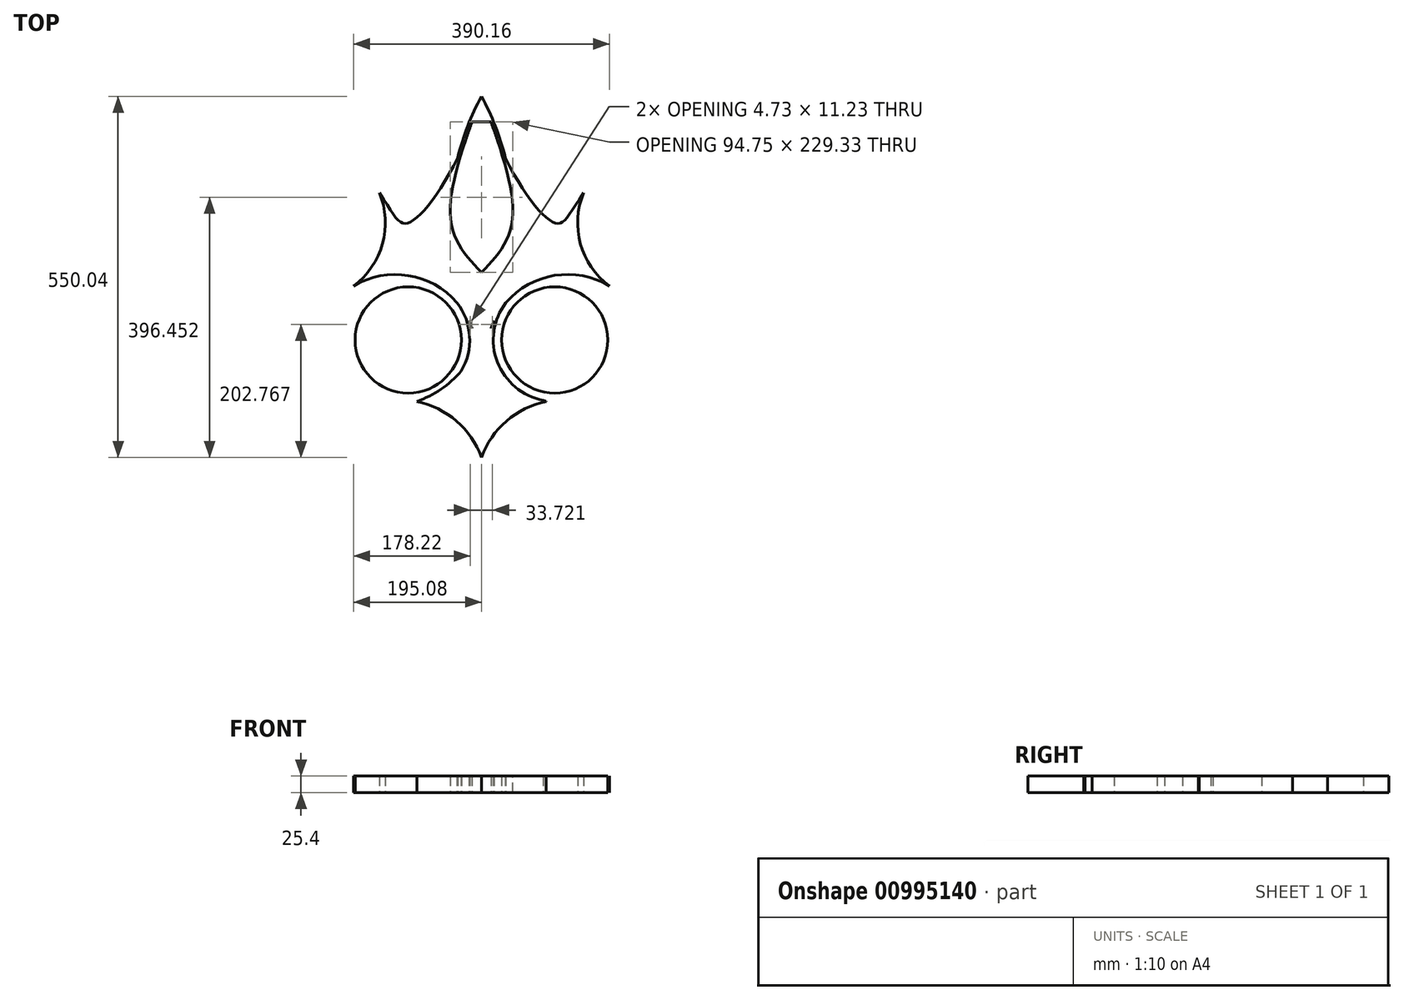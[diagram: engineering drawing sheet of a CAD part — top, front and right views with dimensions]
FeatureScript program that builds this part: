
annotation { "Feature Type Name" : "Feature", "Feature Type Description" : "" }
export const myFeature = defineFeature(function(context is Context, id is Id, definition is map)
    precondition{}
    {
        {
            var Q0;
            Q0=qCreatedBy(makeId("Top.planeOp"),FACE);
            var sketch = newSketch(context, id + "F0", { "sketchPlane" : qUnion([Q0])});
            skFitSpline(sketch, "E0", {"points": [v(0, -75.66) * mm, v(-46.4, 0) * mm, v(0, 192.6) * mm], "startDerivative": vector(-154.45, 162.07) * mm, "endDerivative": vector(135.32, 361.28) * mm});
            skArc(sketch, "E1", {"start": v(-195.08, -96.3) * mm, "mid": v(-150.84, -31.97) * mm, "end": v(-155.67, 45.97) * mm});
            skFitSpline(sketch, "E2", {"points": [v(-155.67, 45.97) * mm, v(-111.61, 0) * mm, v(0, 192.6) * mm], "startDerivative": vector(202, -310.44) * mm, "endDerivative": vector(146.95, 488.71) * mm});
            skCircle(sketch, "E3", {"center": v(-111.61, -178.44) * mm, "radius": 80.9 * mm});
            skArc(sketch, "E4", {"start": v(-98.49, -272) * mm, "mid": v(-61.7, -253.42) * mm, "end": v(-30.96, -225.95) * mm});
            skLineSegment(sketch, "E5", {"start": v(0, 192.6) * mm, "end": v(0, -75.66) * mm});
            skFitSpline(sketch, "E6.MirrorCS", {"points": [v(0, -75.66) * mm, v(46.4, 0) * mm, v(0, 192.6) * mm], "startDerivative": vector(154.45, 162.07) * mm, "endDerivative": vector(-135.32, 361.28) * mm});
            skFitSpline(sketch, "E7.MirrorCS", {"points": [v(155.67, 45.97) * mm, v(111.61, 0) * mm, v(0, 192.6) * mm], "startDerivative": vector(-202, -310.44) * mm, "endDerivative": vector(-146.95, 488.71) * mm});
            skArc(sketch, "E8.MirrorC", {"start": v(195.08, -96.3) * mm, "mid": v(150.84, -31.97) * mm, "end": v(155.67, 45.97) * mm});
            skArc(sketch, "E9.MirrorCS", {"start": v(98.49, -272) * mm, "mid": v(96.3, -271.21) * mm, "end": v(94.13, -270.4) * mm});
            skArc(sketch, "E10.MirrorCS", {"start": v(0, -357.45) * mm, "mid": v(38.14, -301.92) * mm, "end": v(98.49, -272) * mm});
            skPoint(sketch, "E11.startSnap0", {"position": v(-7.64, -189.9) * mm});
            skCircle(sketch, "E12.MirrorC", {"center": v(111.61, -178.44) * mm, "radius": 80.9 * mm});
            skArc(sketch, "E13.MirrorCS", {"start": v(14.5, -160.3) * mm, "mid": v(89.72, -85.77) * mm, "end": v(195.08, -96.3) * mm});
            skLineSegment(sketch, "E14.trimOffspring", {"start": v(0, -189.9) * mm, "end": v(0, -357.45) * mm});
            skPoint(sketch, "E11.start.orphan", {"position": v(0, -189.9) * mm});
            skPoint(sketch, "E15.start.orphan", {"position": v(0, -448.73) * mm});
            skPoint(sketch, "E16.trimOffspring.end.orphan", {"position": v(184.76, -90.76) * mm});
            skPoint(sketch, "E17.1.internal.orphan", {"position": v(-111.61, -28.47) * mm});
            skArc(sketch, "E18.MirrorCS", {"start": v(0, -357.45) * mm, "mid": v(-38.14, -301.92) * mm, "end": v(-98.49, -272) * mm});
            skArc(sketch, "E19.converted", {"start": v(-14.5, -160.3) * mm, "mid": v(-89.72, -85.77) * mm, "end": v(-195.08, -96.3) * mm});
            skPoint(sketch, "E20.orphan", {"position": v(-184.76, -90.76) * mm});
            skArc(sketch, "E21", {"start": v(0, 192.6) * mm, "mid": v(-48.11, 17.83) * mm, "end": v(-14.5, -160.3) * mm});
            skArc(sketch, "E22.MirrorCS", {"start": v(0, 192.6) * mm, "mid": v(48.11, 17.83) * mm, "end": v(14.5, -160.3) * mm});
            skLineSegment(sketch, "E23", {"start": v(-18.45, 153.66) * mm, "end": v(18.45, 153.66) * mm});
            skArc(sketch, "E24.0", {"start": v(-30.96, -225.95) * mm, "mid": v(-22.27, -150.5) * mm, "end": v(-72.4, -93.44) * mm});
            skArc(sketch, "E25.MirrorC", {"start": v(94.13, -270.4) * mm, "mid": v(18.7, -189.85) * mm, "end": v(72.4, -93.44) * mm});
            skPoint(sketch, "E26.orphan", {"position": v(7.64, -189.9) * mm});
            skLineSegment(sketch, "E27", {"start": v(-14.5, -160.3) * mm, "end": v(14.5, -160.3) * mm});
            skSolve(sketch);
        }
        {
            var Q0;
            Q0 = qSketchRegion(id + "F0", true);
            extrude(context, id + "F1", {"entities" : qUnion([Q0]), "depth" : 25.4 * mm, "offsetDistance" : 25.4 * mm});
        }
        {
            var Q0;
            Q0=sQuery(id+"F0.wireOp",EDGE,"E22.MirrorCS");
            var Q1;
            Q1=sQuery(id+"F0.wireOp",EDGE,"E5");
            revolve(context, id + "F2", {"bodyType" : ToolBodyType.SURFACE, "surfaceOperationType" : NewSurfaceOperationType.NEW, "surfaceEntities" : qUnion([Q0]), "axis" : qUnion([Q1]), "revolveType" : RevolveType.ONE_DIRECTION, "oppositeDirection" : true, "angle" : 180 * degree});
        }
    });
